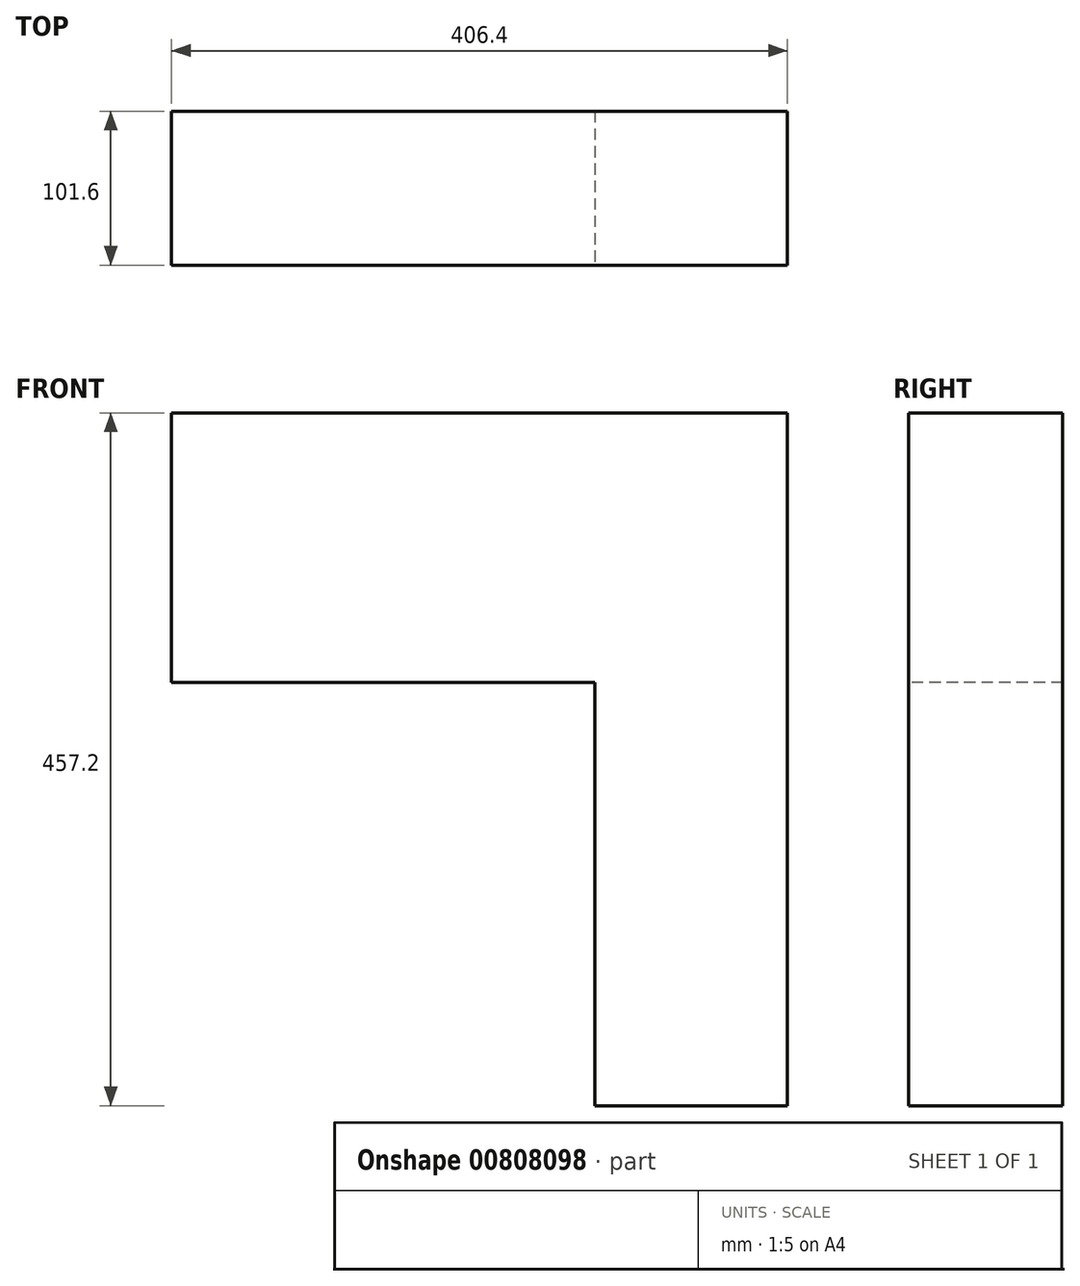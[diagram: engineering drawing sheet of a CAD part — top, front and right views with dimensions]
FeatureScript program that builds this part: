
annotation { "Feature Type Name" : "Feature", "Feature Type Description" : "" }
export const myFeature = defineFeature(function(context is Context, id is Id, definition is map)
    precondition{}
    {
        {
            var Q0;
            Q0=qCreatedBy(makeId("Front.planeOp"),FACE);
            var sketch = newSketch(context, id + "F0", { "sketchPlane" : qUnion([Q0])});
            skLineSegment(sketch, "E0.bottom", {"start": v(228.6, 304.8) * mm, "end": v(-228.6, 304.8) * mm});
            skLineSegment(sketch, "E0.top", {"start": v(228.6, -304.8) * mm, "end": v(-228.6, -304.8) * mm});
            skLineSegment(sketch, "E0.left", {"start": v(228.6, 304.8) * mm, "end": v(228.6, -304.8) * mm});
            skLineSegment(sketch, "E0.right", {"start": v(-228.6, 304.8) * mm, "end": v(-228.6, -304.8) * mm});
            skPoint(sketch, "E0.middle", {"position": v(0, 0) * mm});
            skSolve(sketch);
        }
        {
            var Q0;
            Q0=qSketchRegion(id+"F0",true);
            extrude(context, id + "F1", {"entities" : qUnion([Q0]), "depth" : 101.6 * mm, "offsetDistance" : 25.4 * mm});
        }
        {
            var Q0;
            Q0=makeQuery(id+"F1.opExtrude","CAP_FACE",FACE,{"disambiguationData":[OSD([sQuery(id+"F0.wireOp",EDGE,"E0.bottom"),sQuery(id+"F0.wireOp",EDGE,"E0.top"),sQuery(id+"F0.wireOp",EDGE,"E0.left"),sQuery(id+"F0.wireOp",EDGE,"E0.right")])],"isStart":false});
            var sketch = newSketch(context, id + "F2", { "sketchPlane" : qUnion([Q0])});
            skLineSegment(sketch, "E1.bottom", {"start": v(-177.8, 127) * mm, "end": v(101.6, 127) * mm});
            skLineSegment(sketch, "E1.top", {"start": v(-228.6, -304.8) * mm, "end": v(101.6, -304.8) * mm});
            skLineSegment(sketch, "E1.left", {"start": v(-228.6, 127) * mm, "end": v(-228.6, -304.8) * mm});
            skLineSegment(sketch, "E1.right", {"start": v(101.6, 127) * mm, "end": v(101.6, -152.4) * mm});
            skLineSegment(sketch, "E2.bottom", {"start": v(228.6, -152.4) * mm, "end": v(101.6, -152.4) * mm});
            skLineSegment(sketch, "E2.top", {"start": v(228.6, -304.8) * mm, "end": v(101.6, -304.8) * mm});
            skLineSegment(sketch, "E2.left", {"start": v(228.6, -152.4) * mm, "end": v(228.6, -304.8) * mm});
            skLineSegment(sketch, "E3.top", {"start": v(-228.6, 304.8) * mm, "end": v(-177.8, 304.8) * mm});
            skLineSegment(sketch, "E3.left", {"start": v(-228.6, 127) * mm, "end": v(-228.6, 304.8) * mm});
            skLineSegment(sketch, "E3.right", {"start": v(-177.8, 127) * mm, "end": v(-177.8, 304.8) * mm});
            skSolve(sketch);
        }
        {
            var Q0;
            Q0=makeQuery(id+"F2.imprint","IMPRINT",FACE,{"disambiguationData":[TD([[makeQuery(id+"F2.imprint","IMPRINT",EDGE,{"derivedFrom":sQuery(id+"F2.wireOp",EDGE,"E1.bottom")}),-1.0]])]});
            extrude(context, id + "F3", {"entities" : qUnion([Q0]), "operationType" : NewBodyOperationType.REMOVE, "endBound" : BoundingType.UP_TO_NEXT, "oppositeDirection" : true, "depth" : 25.4 * mm, "offsetDistance" : 25.4 * mm});
        }
    });
